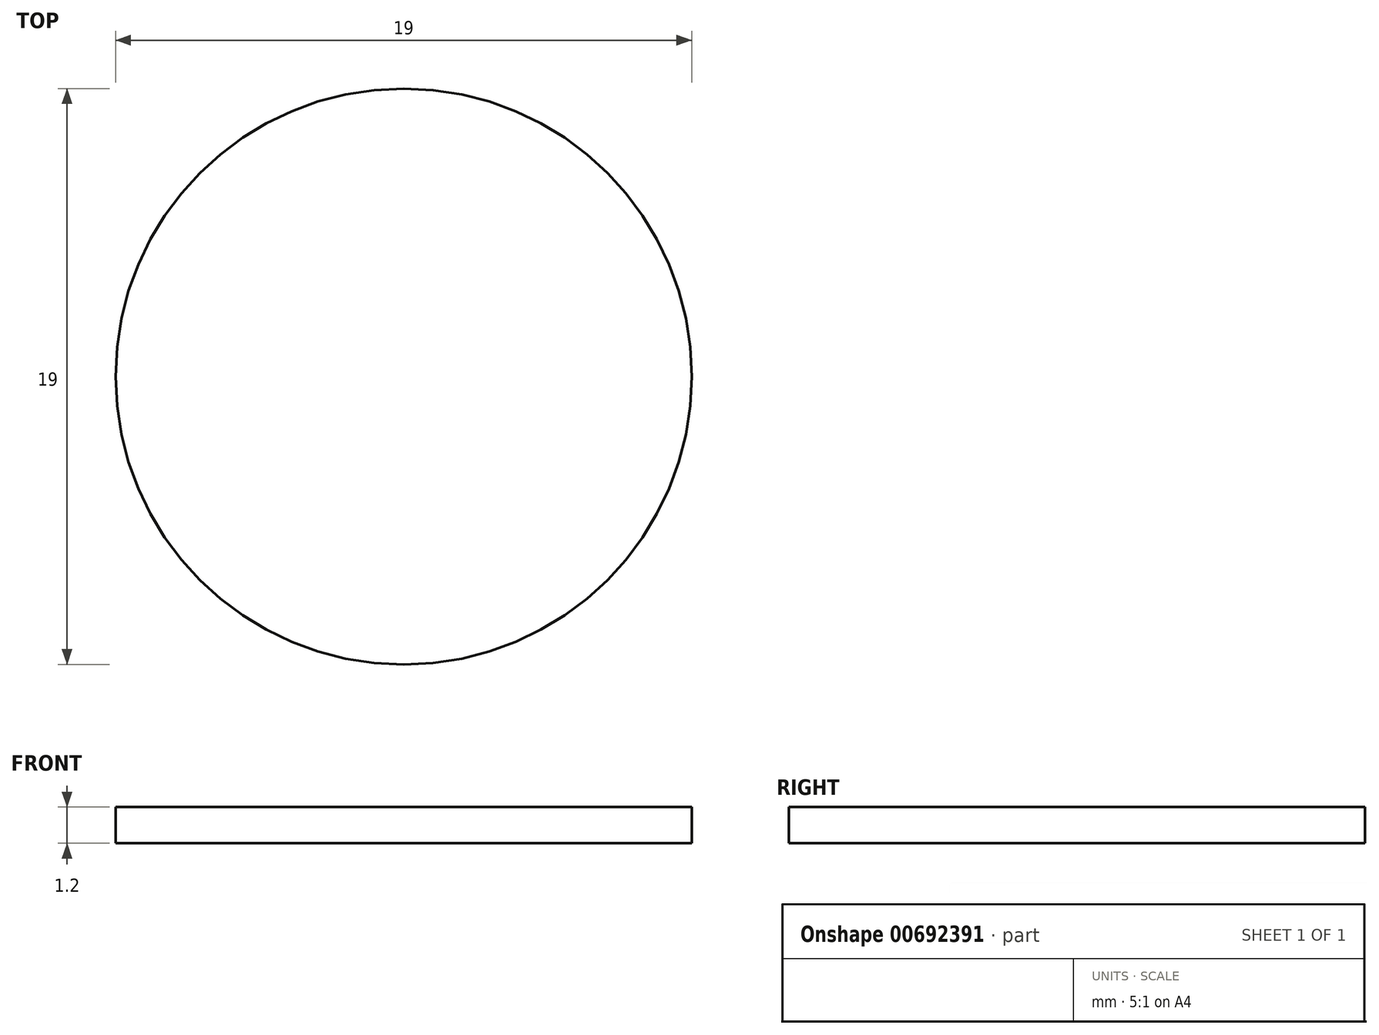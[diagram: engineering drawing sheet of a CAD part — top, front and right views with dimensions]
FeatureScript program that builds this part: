
annotation { "Feature Type Name" : "Feature", "Feature Type Description" : "" }
export const myFeature = defineFeature(function(context is Context, id is Id, definition is map)
    precondition{}
    {
        {
            var Q0;
            Q0=qCreatedBy(makeId("Top.planeOp"),FACE);
            var sketch = newSketch(context, id + "F0", { "sketchPlane" : qUnion([Q0])});
            skCircle(sketch, "E0", {"center": v(0, 0) * mm, "radius": 9.5 * mm});
            skSolve(sketch);
        }
        {
            var Q0;
            Q0=qSketchRegion(id+"F0",true);
            extrude(context, id + "F1", {"entities" : qUnion([Q0]), "depth" : 1.2 * mm, "offsetDistance" : 25 * mm});
        }
    });
